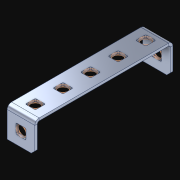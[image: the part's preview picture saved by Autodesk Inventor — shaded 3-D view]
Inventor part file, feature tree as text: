
AUTODESK INVENTOR PART (.ipt)
format: ipt  version: 2021 (Build 250183000, 183)  size: 1,323,520 bytes
history: native  units: in
note: dims shown in document units (in); Inventor stores cm internally (conversion verified against a paired STEP export)
features: extrude x8, other x8, sketch x4, pattern_linear x3
ambient origin geometry x8: Origin, YZ Plane, XZ Plane, XY Plane, X Axis, Y Axis, Z Axis, Center Point
bodies: Solid1 (feature_tree)
feature tree (23):
  pattern_linear  "Rectangular Pattern1"  Spacing1=0.182in  [1 undecoded]
  pattern_linear  "Rectangular Pattern2"  Spacing1=0.046in  [1 undecoded]
  pattern_linear  "Rectangular Pattern3"  Spacing1=0.5in  [1 undecoded]
  extrude  "Extrusion1"  Depth=0.3937in
  sketch  "Sketch1"  dims[d0=0.182in]
  other  "Srf1"
  sketch  "Sketch2"  dims[d1=0.046in d2=0.0in]
  other  "Srf2"
  sketch  "Sketch3"  dims[d3=0.182in]
  other  "Srf3"
  other  "Srf72"
  other  "Srf107"
  other  "Srf142"
  other  "Srf177"
  sketch  "Sketch4"  dims[d4=0.046in d5=0.0in d6=0.182in d7=0.046in d8=0.0in d11=0.5in d12=0.3937in d14=0.5in d15=1.9685in d17=0.5in d18=0.3937in d20=0.5in d21=17.0in d22=0.0in]
  parser-record x1  (decoder bookkeeping rows leaked as tree rows — omitted from the tree; the rows remain in map.json)
  extrude  "ExtrusionSrf1"  Depth=0.5in
  extrude  "ExtrusionSrf2"  Depth=0.5in
  extrude  "ExtrusionSrf3"  Depth=0.3937in
  extrude  "ExtrusionSrf72"  Depth=0.5in
  extrude  "ExtrusionSrf107"  Depth=0.5in
  extrude  "ExtrusionSrf142"  TaperAngle=0.0deg  [1 undecoded]
  extrude  "ExtrusionSrf177"  [1 undecoded]
note: 5 required parameter values undecoded (feature->parameter linkage not recoverable at this tier; creation-order binding heuristic only, values carry confidence <= 0.55)
